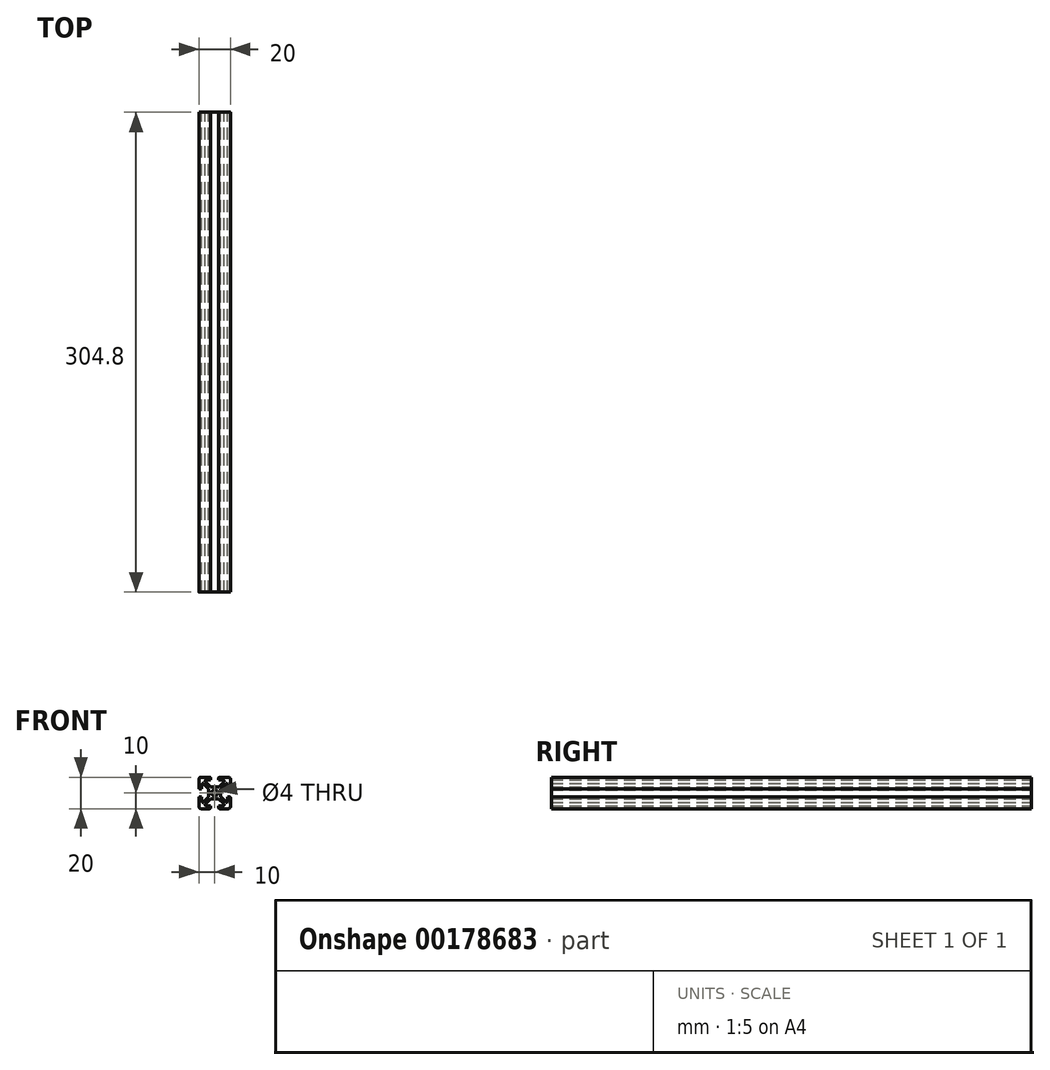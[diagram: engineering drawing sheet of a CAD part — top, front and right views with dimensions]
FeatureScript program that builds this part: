
annotation { "Feature Type Name" : "Feature", "Feature Type Description" : "" }
export const myFeature = defineFeature(function(context is Context, id is Id, definition is map)
    precondition{}
    {
        {
            var Q0;
            Q0=qCreatedBy(makeId("Front.planeOp"),FACE);
            var sketch = newSketch(context, id + "F0", { "sketchPlane" : qUnion([Q0])});
            skLineSegment(sketch, "E0.bottom", {"start": v(0, 0) * mm, "end": v(-20, 0) * mm, "construction": true});
            skLineSegment(sketch, "E0.top", {"start": v(0, 20) * mm, "end": v(-20, 20) * mm, "construction": true});
            skLineSegment(sketch, "E0.left", {"start": v(0, 0) * mm, "end": v(0, 20) * mm, "construction": true});
            skLineSegment(sketch, "E0.right", {"start": v(-20, 0) * mm, "end": v(-20, 20) * mm, "construction": true});
            skCircle(sketch, "E1", {"center": v(-10, 10) * mm, "radius": 2 * mm});
            skLineSegment(sketch, "E2", {"start": v(-18.73, 20) * mm, "end": v(-13.14, 20) * mm});
            skLineSegment(sketch, "E3", {"start": v(-12.5, 19.37) * mm, "end": v(-12.5, 18.2) * mm});
            skLineSegment(sketch, "E4", {"start": v(-12.5, 18.2) * mm, "end": v(-15.4, 18.2) * mm});
            skLineSegment(sketch, "E5", {"start": v(-15.84, 17.12) * mm, "end": v(-12.69, 13.96) * mm});
            skLineSegment(sketch, "E6", {"start": v(-12.24, 13.77) * mm, "end": v(-10, 13.77) * mm});
            skLineSegment(sketch, "E7", {"start": v(-10, 20) * mm, "end": v(-10, 0) * mm, "construction": true});
            skLineSegment(sketch, "E8", {"start": v(-20, 10) * mm, "end": v(0, 10) * mm, "construction": true});
            skLineSegment(sketch, "E9", {"start": v(-20, 18.73) * mm, "end": v(-20, 13.13) * mm});
            skLineSegment(sketch, "E10", {"start": v(-19.37, 12.5) * mm, "end": v(-18.2, 12.5) * mm});
            skLineSegment(sketch, "E11", {"start": v(-18.2, 12.5) * mm, "end": v(-18.2, 15.4) * mm});
            skLineSegment(sketch, "E12", {"start": v(-17.12, 15.84) * mm, "end": v(-13.96, 12.69) * mm});
            skLineSegment(sketch, "E13", {"start": v(-13.77, 12.24) * mm, "end": v(-13.77, 10) * mm});
            skLineSegment(sketch, "E14.MirrorCS", {"start": v(-7.76, 13.77) * mm, "end": v(-10, 13.77) * mm});
            skLineSegment(sketch, "E15.MirrorCS", {"start": v(-4.16, 17.12) * mm, "end": v(-7.31, 13.96) * mm});
            skLineSegment(sketch, "E16.MirrorCS", {"start": v(-7.5, 18.2) * mm, "end": v(-4.6, 18.2) * mm});
            skLineSegment(sketch, "E17.MirrorCS", {"start": v(-7.5, 19.37) * mm, "end": v(-7.5, 18.2) * mm});
            skLineSegment(sketch, "E18.MirrorCS", {"start": v(-1.27, 20) * mm, "end": v(-6.87, 20) * mm});
            skLineSegment(sketch, "E19.MirrorCS", {"start": v(0, 18.73) * mm, "end": v(0, 13.13) * mm});
            skLineSegment(sketch, "E20.MirrorCS", {"start": v(-0.63, 12.5) * mm, "end": v(-1.8, 12.5) * mm});
            skLineSegment(sketch, "E21.MirrorCS", {"start": v(-1.8, 12.5) * mm, "end": v(-1.8, 15.4) * mm});
            skLineSegment(sketch, "E22.MirrorCS", {"start": v(-2.88, 15.84) * mm, "end": v(-6.04, 12.69) * mm});
            skLineSegment(sketch, "E23.MirrorCS", {"start": v(-6.23, 12.24) * mm, "end": v(-6.23, 10) * mm});
            skLineSegment(sketch, "E24.MirrorCS", {"start": v(-13.77, 7.5) * mm, "end": v(-13.77, 10) * mm});
            skLineSegment(sketch, "E25.MirrorCS", {"start": v(-17.12, 4.16) * mm, "end": v(-13.77, 7.5) * mm});
            skLineSegment(sketch, "E26.MirrorCS", {"start": v(-18.2, 7.5) * mm, "end": v(-18.2, 4.6) * mm});
            skLineSegment(sketch, "E27.MirrorCS", {"start": v(-19.37, 7.5) * mm, "end": v(-18.2, 7.5) * mm});
            skLineSegment(sketch, "E28.MirrorCS", {"start": v(-20, 1.27) * mm, "end": v(-20, 6.87) * mm});
            skLineSegment(sketch, "E29.MirrorCS", {"start": v(-18.73, 0) * mm, "end": v(-13.14, 0) * mm});
            skLineSegment(sketch, "E30.MirrorCS", {"start": v(-12.5, 0.64) * mm, "end": v(-12.5, 1.8) * mm});
            skLineSegment(sketch, "E31.MirrorCS", {"start": v(-12.5, 1.8) * mm, "end": v(-15.4, 1.8) * mm});
            skLineSegment(sketch, "E32.MirrorCS", {"start": v(-15.84, 2.88) * mm, "end": v(-12.69, 6.04) * mm});
            skLineSegment(sketch, "E33.MirrorCS", {"start": v(-12.24, 6.23) * mm, "end": v(-10, 6.23) * mm});
            skLineSegment(sketch, "E34.MirrorCS", {"start": v(-7.5, 6.23) * mm, "end": v(-10, 6.23) * mm});
            skLineSegment(sketch, "E35.MirrorCS", {"start": v(-4.16, 2.88) * mm, "end": v(-7.5, 6.23) * mm});
            skLineSegment(sketch, "E36.MirrorCS", {"start": v(-7.5, 1.8) * mm, "end": v(-4.6, 1.8) * mm});
            skLineSegment(sketch, "E37.MirrorCS", {"start": v(-7.5, 0.63) * mm, "end": v(-7.5, 1.8) * mm});
            skLineSegment(sketch, "E38.MirrorCS", {"start": v(-1.27, 0) * mm, "end": v(-6.87, 0) * mm});
            skLineSegment(sketch, "E39.MirrorCS", {"start": v(0, 1.27) * mm, "end": v(0, 6.87) * mm});
            skLineSegment(sketch, "E40.MirrorCS", {"start": v(-0.64, 7.5) * mm, "end": v(-1.8, 7.5) * mm});
            skLineSegment(sketch, "E41.MirrorCS", {"start": v(-1.8, 7.5) * mm, "end": v(-1.8, 4.6) * mm});
            skLineSegment(sketch, "E42.MirrorCS", {"start": v(-2.88, 4.16) * mm, "end": v(-6.04, 7.31) * mm});
            skLineSegment(sketch, "E43.MirrorCS", {"start": v(-6.23, 7.76) * mm, "end": v(-6.23, 10) * mm});
            skPoint(sketch, "E44.visualSharp", {"position": v(-20, 20) * mm});
            skArc(sketch, "E44.filletArc", {"start": v(-18.73, 20) * mm, "mid": v(-19.63, 19.63) * mm, "end": v(-20, 18.73) * mm});
            skPoint(sketch, "E45.visualSharp", {"position": v(-20, 0) * mm});
            skArc(sketch, "E45.filletArc", {"start": v(-20, 1.27) * mm, "mid": v(-19.63, 0.37) * mm, "end": v(-18.73, 0) * mm});
            skPoint(sketch, "E46.visualSharp", {"position": v(0, 0) * mm});
            skArc(sketch, "E46.filletArc", {"start": v(-1.27, 0) * mm, "mid": v(-0.37, 0.37) * mm, "end": v(0, 1.27) * mm});
            skPoint(sketch, "E47.visualSharp", {"position": v(0, 20) * mm});
            skArc(sketch, "E47.filletArc", {"start": v(0, 18.73) * mm, "mid": v(-0.37, 19.63) * mm, "end": v(-1.27, 20) * mm});
            skPoint(sketch, "E48.visualSharp", {"position": v(-16.93, 18.2) * mm});
            skArc(sketch, "E48.filletArc", {"start": v(-15.4, 18.2) * mm, "mid": v(-15.98, 17.8) * mm, "end": v(-15.84, 17.12) * mm});
            skPoint(sketch, "E49.visualSharp", {"position": v(-18.2, 16.93) * mm});
            skArc(sketch, "E49.filletArc", {"start": v(-17.12, 15.84) * mm, "mid": v(-17.8, 15.98) * mm, "end": v(-18.2, 15.4) * mm});
            skPoint(sketch, "E50.visualSharp", {"position": v(-18.2, 3.07) * mm});
            skArc(sketch, "E50.filletArc", {"start": v(-18.2, 4.6) * mm, "mid": v(-17.8, 4.02) * mm, "end": v(-17.12, 4.16) * mm});
            skPoint(sketch, "E51.visualSharp", {"position": v(-16.93, 1.8) * mm});
            skArc(sketch, "E51.filletArc", {"start": v(-15.84, 2.88) * mm, "mid": v(-15.98, 2.2) * mm, "end": v(-15.4, 1.8) * mm});
            skPoint(sketch, "E52.visualSharp", {"position": v(-3.07, 1.8) * mm});
            skArc(sketch, "E52.filletArc", {"start": v(-4.6, 1.8) * mm, "mid": v(-4.02, 2.2) * mm, "end": v(-4.16, 2.88) * mm});
            skPoint(sketch, "E53.visualSharp", {"position": v(-1.8, 3.07) * mm});
            skArc(sketch, "E53.filletArc", {"start": v(-2.88, 4.16) * mm, "mid": v(-2.2, 4.02) * mm, "end": v(-1.8, 4.6) * mm});
            skPoint(sketch, "E54.visualSharp", {"position": v(-1.8, 16.93) * mm});
            skArc(sketch, "E54.filletArc", {"start": v(-1.8, 15.4) * mm, "mid": v(-2.2, 15.98) * mm, "end": v(-2.88, 15.84) * mm});
            skPoint(sketch, "E55.visualSharp", {"position": v(-3.07, 18.2) * mm});
            skArc(sketch, "E55.filletArc", {"start": v(-4.16, 17.12) * mm, "mid": v(-4.02, 17.8) * mm, "end": v(-4.6, 18.2) * mm});
            skPoint(sketch, "E56.visualSharp", {"position": v(-20, 12.5) * mm});
            skArc(sketch, "E56.filletArc", {"start": v(-20, 13.13) * mm, "mid": v(-19.81, 12.69) * mm, "end": v(-19.37, 12.5) * mm});
            skPoint(sketch, "E57.visualSharp", {"position": v(-20, 7.5) * mm});
            skArc(sketch, "E57.filletArc", {"start": v(-19.37, 7.5) * mm, "mid": v(-19.81, 7.31) * mm, "end": v(-20, 6.87) * mm});
            skPoint(sketch, "E58.visualSharp", {"position": v(-12.5, 0) * mm});
            skArc(sketch, "E58.filletArc", {"start": v(-13.14, 0) * mm, "mid": v(-12.69, 0.19) * mm, "end": v(-12.5, 0.64) * mm});
            skPoint(sketch, "E59.visualSharp", {"position": v(-7.5, 0) * mm});
            skArc(sketch, "E59.filletArc", {"start": v(-7.5, 0.63) * mm, "mid": v(-7.31, 0.19) * mm, "end": v(-6.87, 0) * mm});
            skPoint(sketch, "E60.visualSharp", {"position": v(0, 7.5) * mm});
            skArc(sketch, "E60.filletArc", {"start": v(0, 6.87) * mm, "mid": v(-0.19, 7.31) * mm, "end": v(-0.64, 7.5) * mm});
            skPoint(sketch, "E61.visualSharp", {"position": v(0, 12.5) * mm});
            skArc(sketch, "E61.filletArc", {"start": v(-0.63, 12.5) * mm, "mid": v(-0.19, 12.69) * mm, "end": v(0, 13.13) * mm});
            skPoint(sketch, "E62.visualSharp", {"position": v(-7.5, 20) * mm});
            skArc(sketch, "E62.filletArc", {"start": v(-6.87, 20) * mm, "mid": v(-7.31, 19.81) * mm, "end": v(-7.5, 19.37) * mm});
            skPoint(sketch, "E63.visualSharp", {"position": v(-12.5, 20) * mm});
            skArc(sketch, "E63.filletArc", {"start": v(-12.5, 19.37) * mm, "mid": v(-12.69, 19.81) * mm, "end": v(-13.14, 20) * mm});
            skPoint(sketch, "E64.visualSharp", {"position": v(-12.5, 13.77) * mm});
            skArc(sketch, "E64.filletArc", {"start": v(-12.69, 13.96) * mm, "mid": v(-12.48, 13.82) * mm, "end": v(-12.24, 13.77) * mm});
            skPoint(sketch, "E65.visualSharp", {"position": v(-7.5, 13.77) * mm});
            skArc(sketch, "E65.filletArc", {"start": v(-7.76, 13.77) * mm, "mid": v(-7.52, 13.82) * mm, "end": v(-7.31, 13.96) * mm});
            skPoint(sketch, "E66.visualSharp", {"position": v(-6.23, 12.5) * mm});
            skArc(sketch, "E66.filletArc", {"start": v(-6.04, 12.69) * mm, "mid": v(-6.18, 12.48) * mm, "end": v(-6.23, 12.24) * mm});
            skPoint(sketch, "E67.visualSharp", {"position": v(-6.23, 7.5) * mm});
            skArc(sketch, "E67.filletArc", {"start": v(-6.23, 7.76) * mm, "mid": v(-6.18, 7.52) * mm, "end": v(-6.04, 7.31) * mm});
            skPoint(sketch, "E68.visualSharp", {"position": v(-12.5, 6.23) * mm});
            skArc(sketch, "E68.filletArc", {"start": v(-12.24, 6.23) * mm, "mid": v(-12.48, 6.18) * mm, "end": v(-12.69, 6.04) * mm});
            skPoint(sketch, "E69.visualSharp", {"position": v(-13.77, 12.5) * mm});
            skArc(sketch, "E69.filletArc", {"start": v(-13.77, 12.24) * mm, "mid": v(-13.82, 12.48) * mm, "end": v(-13.96, 12.69) * mm});
            skSolve(sketch);
        }
        {
            var Q0;
            Q0 = qSketchRegion(id + "F0", true);
            extrude(context, id + "F1", {"entities" : qUnion([Q0]), "depth" : 304.8 * mm});
        }
    });
